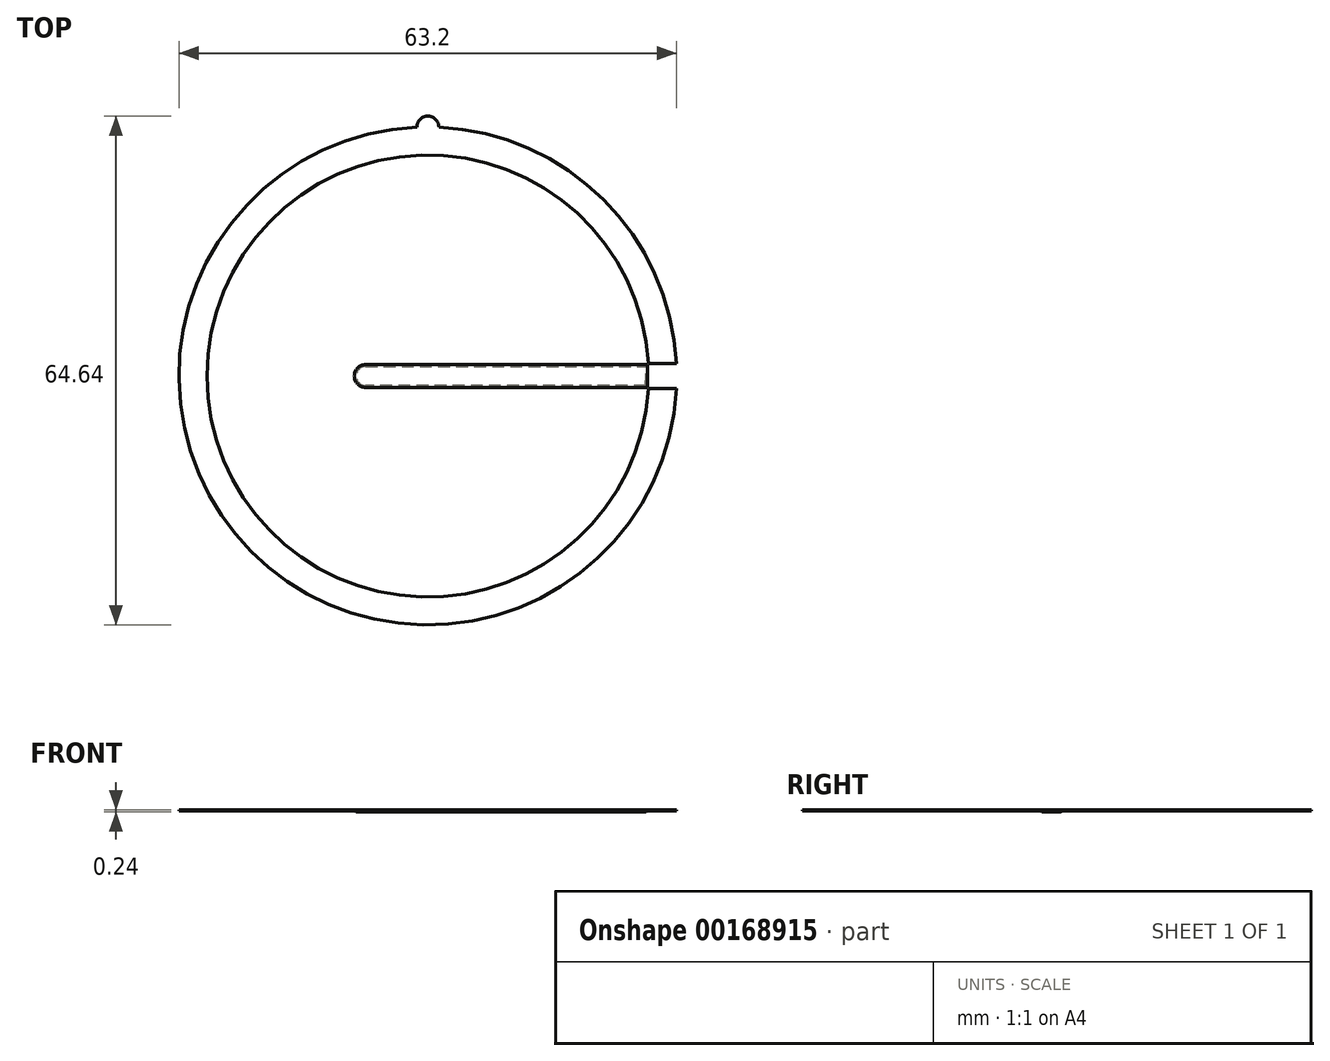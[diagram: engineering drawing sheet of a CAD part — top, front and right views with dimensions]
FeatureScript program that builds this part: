
annotation { "Feature Type Name" : "Feature", "Feature Type Description" : "" }
export const myFeature = defineFeature(function(context is Context, id is Id, definition is map)
    precondition{}
    {
        {
            assignVariable(context, id + "F0", {"name" : "large_t", "anyValue" : .11});
        }
        {
            assignVariable(context, id + "F1", {"name" : "small_t", "anyValue" : 0.12});
        }
        {
            var Q0;
            Q0=qCreatedBy(makeId("Top.planeOp"),FACE);
            var sketch = newSketch(context, id + "F2", { "sketchPlane" : qUnion([Q0])});
            skCircle(sketch, "E0", {"center": v(0, 0) * mm, "radius": 31.62 * mm});
            skCircle(sketch, "E1", {"center": v(0, 0) * mm, "radius": 28.07 * mm});
            skCircle(sketch, "E2", {"center": v(0, 31.62) * mm, "radius": 1.4 * mm});
            skLineSegment(sketch, "E3", {"start": v(31.62, 0) * mm, "end": v(-7.9, 0) * mm, "construction": true});
            skArc(sketch, "E4.0.startCap", {"start": v(31.62, 1.59) * mm, "mid": v(33.21, 0) * mm, "end": v(31.62, -1.59) * mm});
            skArc(sketch, "E4.0.endCap", {"start": v(-7.9, -1.59) * mm, "mid": v(-9.5, 0) * mm, "end": v(-7.9, 1.59) * mm});
            skLineSegment(sketch, "E4.0.left", {"start": v(31.62, -1.59) * mm, "end": v(-7.9, -1.59) * mm});
            skLineSegment(sketch, "E4.0.right", {"start": v(31.62, 1.59) * mm, "end": v(-7.9, 1.59) * mm});
            skSolve(sketch);
        }
        {
            var Q0;
            {var subQ0=sQuery(id+"F2.wireOp",EDGE,"E2");var subQ1=sQuery(id+"F2.wireOp",EDGE,"E0");var subQ2=makeQuery(id+"F2.imprint","INTERSECT",VERTEX,{"disambiguationData":[OD(0.0)],"derivedFrom":[subQ1,subQ0]});Q0=makeQuery(id+"F2.imprint","IMPRINT",FACE,{"disambiguationData":[TD([[makeQuery(id+"F2.imprint","IMPRINT",EDGE,{"disambiguationData":[TD([[subQ2,1.0]])],"derivedFrom":subQ1}),1.0]])]});}
            var Q1;
            {var subQ5=sQuery(id+"F2.wireOp",EDGE,"E4.0.endCap");Q1=makeQuery(id+"F2.imprint","IMPRINT",FACE,{"disambiguationData":[TD([[makeQuery(id+"F2.imprint","IMPRINT",EDGE,{"derivedFrom":subQ5}),1.0]])]});}
            var Q2;
            {var subQ0=sQuery(id+"F2.wireOp",EDGE,"E2");var subQ1=sQuery(id+"F2.wireOp",EDGE,"E0");var subQ2=makeQuery(id+"F2.imprint","INTERSECT",VERTEX,{"disambiguationData":[OD(0.0)],"derivedFrom":[subQ1,subQ0]});Q2=makeQuery(id+"F2.imprint","IMPRINT",FACE,{"disambiguationData":[TD([[makeQuery(id+"F2.imprint","IMPRINT",EDGE,{"disambiguationData":[TD([[subQ2,-1.0]])],"derivedFrom":subQ1}),-1.0]])]});}
            var Q3;
            {var subQ0=sQuery(id+"F2.wireOp",EDGE,"E2");var subQ1=sQuery(id+"F2.wireOp",EDGE,"E0");var subQ2=makeQuery(id+"F2.imprint","INTERSECT",VERTEX,{"disambiguationData":[OD(0.0)],"derivedFrom":[subQ1,subQ0]});Q3=makeQuery(id+"F2.imprint","IMPRINT",FACE,{"disambiguationData":[TD([[makeQuery(id+"F2.imprint","IMPRINT",EDGE,{"disambiguationData":[TD([[subQ2,-1.0]])],"derivedFrom":subQ1}),1.0]])]});}
            extrude(context, id + "F3", {"entities" : qUnion([Q0, Q1, Q2, Q3]), "depth" : (getVariable(context, 'large_t')) * mm});
        }
        {
            var Q0;
            {var subQ5=sQuery(id+"F2.wireOp",EDGE,"E4.0.endCap");Q0=makeQuery(id+"F2.imprint","IMPRINT",FACE,{"disambiguationData":[TD([[makeQuery(id+"F2.imprint","IMPRINT",EDGE,{"derivedFrom":subQ5}),1.0]])]});}
            extrude(context, id + "F4", {"entities" : qUnion([Q0]), "operationType" : NewBodyOperationType.ADD, "oppositeDirection" : true, "depth" : (getVariable(context, 'small_t')) * mm});
        }
        {
            var Q0;
            Q0=makeQuery(id+"F4.opExtrude","CAP_EDGE",EDGE,{"disambiguationData":[OSD([sQuery(id+"F2.wireOp",EDGE,"E1")])],"isStart":false});
            var Q1;
            {var subQ0=sQuery(id+"F2.wireOp",EDGE,"E0");Q1=makeQuery(id+"F3.opExtrude","CAP_EDGE",EDGE,{"disambiguationData":[OSD([subQ0]),TDD([makeQuery(id+"F2.imprint","IMPRINT",EDGE,{"disambiguationData":[TD([[makeQuery(id+"F2.imprint","INTERSECT",VERTEX,{"disambiguationData":[OD(1.0)],"derivedFrom":[subQ0,sQuery(id+"F2.wireOp",EDGE,"E2")]}),-1.0]])],"derivedFrom":subQ0})])],"isStart":true});}
            var Q2;
            {var subQ0=sQuery(id+"F2.wireOp",EDGE,"E0");Q2=makeQuery(id+"F3.opExtrude","CAP_EDGE",EDGE,{"disambiguationData":[OSD([subQ0]),TDD([makeQuery(id+"F2.imprint","IMPRINT",EDGE,{"disambiguationData":[TD([[makeQuery(id+"F2.imprint","INTERSECT",VERTEX,{"disambiguationData":[OD(0.0)],"derivedFrom":[subQ0,sQuery(id+"F2.wireOp",EDGE,"E2")]}),1.0]])],"derivedFrom":subQ0})])],"isStart":false});}
            var Q3;
            {var subQ0=sQuery(id+"F2.wireOp",EDGE,"E0");Q3=makeQuery(id+"F3.opExtrude","CAP_EDGE",EDGE,{"disambiguationData":[OSD([subQ0]),TDD([makeQuery(id+"F2.imprint","IMPRINT",EDGE,{"disambiguationData":[TD([[makeQuery(id+"F2.imprint","INTERSECT",VERTEX,{"disambiguationData":[OD(1.0)],"derivedFrom":[subQ0,sQuery(id+"F2.wireOp",EDGE,"E2")]}),-1.0]])],"derivedFrom":subQ0})])],"isStart":false});}
            var Q4;
            Q4=makeQuery(id+"F3.opExtrude","CAP_EDGE",EDGE,{"disambiguationData":[OSD([sQuery(id+"F2.wireOp",EDGE,"E2")])],"isStart":true});
            var Q5;
            Q5=makeQuery(id+"F3.opExtrude","CAP_EDGE",EDGE,{"disambiguationData":[OSD([sQuery(id+"F2.wireOp",EDGE,"E2")])],"isStart":false});
            var Q6;
            {var subQ0=sQuery(id+"F2.wireOp",EDGE,"E0");Q6=makeQuery(id+"F3.opExtrude","CAP_EDGE",EDGE,{"disambiguationData":[OSD([subQ0]),TDD([makeQuery(id+"F2.imprint","IMPRINT",EDGE,{"disambiguationData":[TD([[makeQuery(id+"F2.imprint","INTERSECT",VERTEX,{"disambiguationData":[OD(0.0)],"derivedFrom":[subQ0,sQuery(id+"F2.wireOp",EDGE,"E2")]}),1.0]])],"derivedFrom":subQ0})])],"isStart":true});}
            var Q7;
            Q7=makeQuery(id+"F4.opExtrude","CAP_EDGE",EDGE,{"disambiguationData":[OSD([sQuery(id+"F2.wireOp",EDGE,"E4.0.right")])],"isStart":false});
            var Q8;
            Q8=makeQuery(id+"F4.opExtrude","CAP_EDGE",EDGE,{"disambiguationData":[OSD([sQuery(id+"F2.wireOp",EDGE,"E4.0.endCap")])],"isStart":false});
            var Q9;
            Q9=makeQuery(id+"F4.opExtrude","CAP_EDGE",EDGE,{"disambiguationData":[OSD([sQuery(id+"F2.wireOp",EDGE,"E4.0.left")])],"isStart":false});
            var Q10;
            Q10=makeQuery(id+"F3.opExtrude","CAP_FACE",FACE,{"disambiguationData":[OSD([sQuery(id+"F2.wireOp",EDGE,"E0"),sQuery(id+"F2.wireOp",EDGE,"E2"),sQuery(id+"F2.wireOp",EDGE,"E4.0.endCap"),sQuery(id+"F2.wireOp",EDGE,"E4.0.left"),sQuery(id+"F2.wireOp",EDGE,"E4.0.right")])],"isStart":false});
            var Q11;
            Q11=makeQuery(id+"F3.opExtrude","SWEPT_EDGE",EDGE,{"disambiguationData":[OSD([sQuery(id+"F2.wireOp",EDGE,"E0"),sQuery(id+"F2.wireOp",EDGE,"E4.0.left")])]});
            var Q12;
            Q12=makeQuery(id+"F3.opExtrude","SWEPT_EDGE",EDGE,{"disambiguationData":[OSD([sQuery(id+"F2.wireOp",EDGE,"E0"),sQuery(id+"F2.wireOp",EDGE,"E4.0.right")])]});
            chamfer(context, id + "F5", {"entities" : qUnion([Q0, Q1, Q2, Q3, Q4, Q5, Q6, Q7, Q8, Q9, Q10, Q11, Q12]), "width" : 0.38 * mm, "tangentPropagation" : true});
        }
    });
